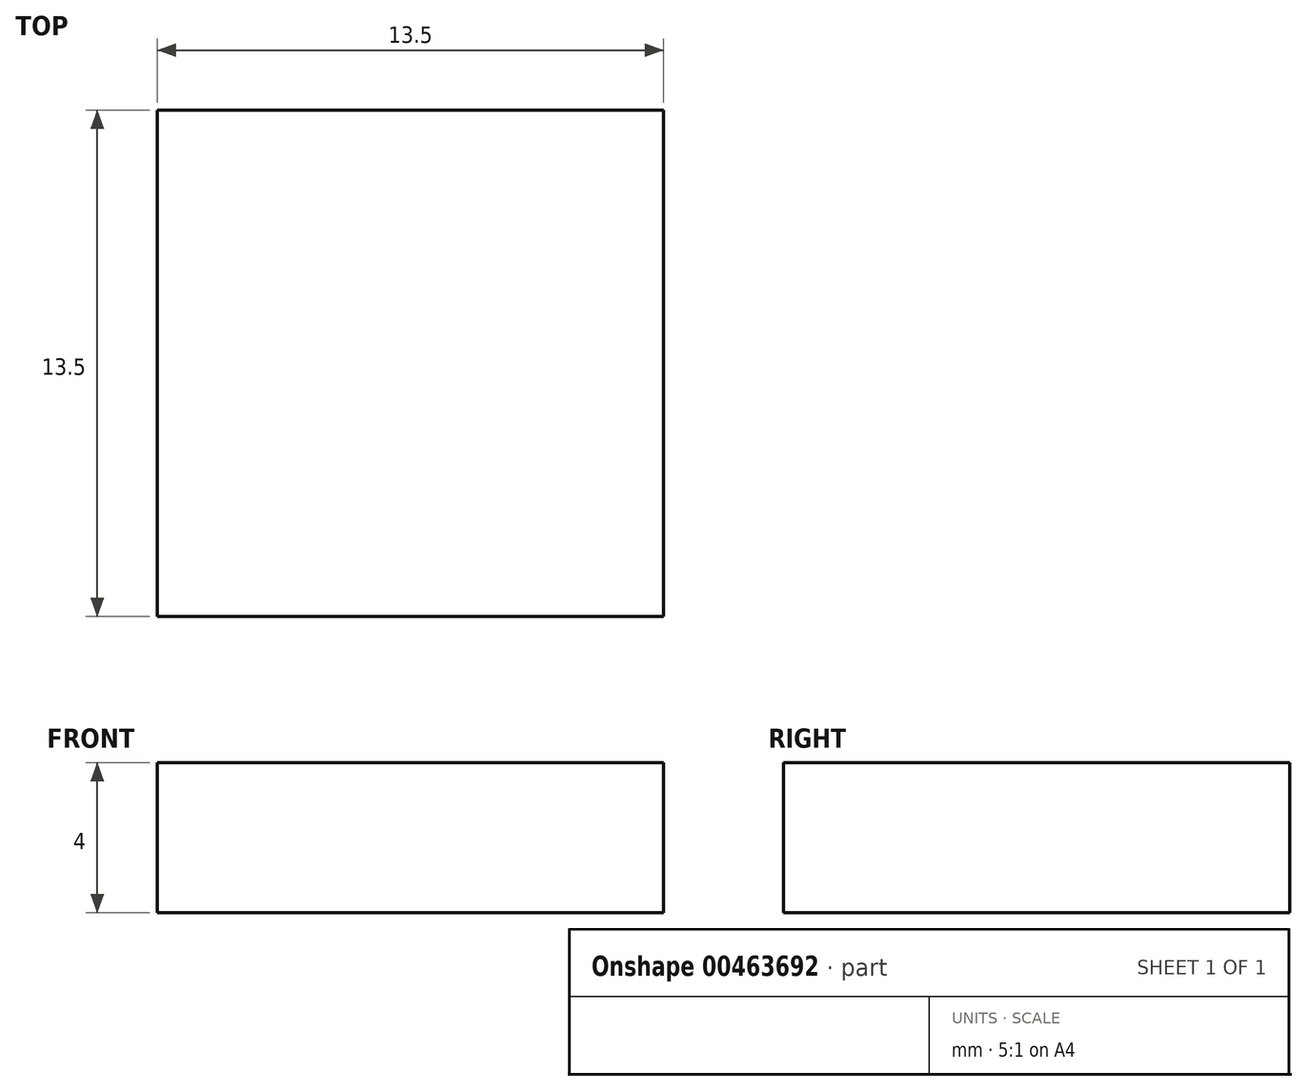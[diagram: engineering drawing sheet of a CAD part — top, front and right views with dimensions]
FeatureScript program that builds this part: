
annotation { "Feature Type Name" : "Feature", "Feature Type Description" : "" }
export const myFeature = defineFeature(function(context is Context, id is Id, definition is map)
    precondition{}
    {
        {
            var Q0;
            Q0=qCreatedBy(makeId("Top.planeOp"),FACE);
            var sketch = newSketch(context, id + "F0", { "sketchPlane" : qUnion([Q0])});
            skLineSegment(sketch, "E0.bottom", {"start": v(-17.52, 17.3) * mm, "end": v(-4.02, 17.3) * mm});
            skLineSegment(sketch, "E0.top", {"start": v(-17.52, 3.8) * mm, "end": v(-4.02, 3.8) * mm});
            skLineSegment(sketch, "E0.left", {"start": v(-17.52, 17.3) * mm, "end": v(-17.52, 3.8) * mm});
            skLineSegment(sketch, "E0.right", {"start": v(-4.02, 17.3) * mm, "end": v(-4.02, 3.8) * mm});
            skSolve(sketch);
        }
        {
            var Q0;
            Q0 = qSketchRegion(id + "F0", true);
            extrude(context, id + "F1", {"entities" : qUnion([Q0]), "depth" : 4 * mm});
        }
    });
